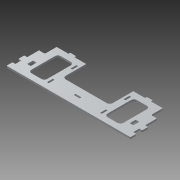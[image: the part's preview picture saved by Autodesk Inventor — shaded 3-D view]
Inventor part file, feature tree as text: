
AUTODESK INVENTOR PART (.ipt)
format: ipt  version: 2015 (Build 190159000, 159)  size: 278,016 bytes
history: native  units: mm
features: extrude x1, sketch x1
ambient origin geometry x8: Origin, YZ Plane, XZ Plane, XY Plane, X Axis, Y Axis, Z Axis, Center Point
bodies: Body1 (feature_tree)
feature tree (2):
  extrude  "Extrusion8"  Depth=40.0mm
  sketch  "Sketch1"  dims[d0=80.0mm d1=40.0mm d2=50.0mm d10=50.0mm d15=3.0mm d16=10.0mm d18=10.0mm d20=3.0mm d23=40.0mm d24=40.0mm d27=1.0mm d28=10.0mm d29=6.0mm d31=40.0mm d32=10.0mm d33=6.0mm d35=40.0mm d39=10.0mm d40=3.0mm d41=10.0mm d42=3.0mm d44=10.0mm d45=10.0mm d50=3.0mm d51=10.0mm d52=10.0mm d54=3.0mm d55=10.0mm d56=10.0mm d60=10.0mm d61=3.0mm d62=17.0mm d66=40.0mm d67=40.0mm d71=3.5mm d72=3.5mm d73=3.5mm d74=3.5mm d77=20.0mm d78=20.0mm d79=10.0mm d80=10.0mm d81=2.0mm d82=10.0mm d84=50.0mm d85=20.0mm d86=20.0mm d87=60.0mm d88=5.0mm d92=30.0mm d93=5.0mm d94=30.0mm d95=1.0mm d96=5.0mm d97=10.0mm d98=10.0mm d99=1.0mm d100=10.0mm d101=10.0mm d102=5.0mm d103=5.0mm d104=210.0mm d105=1.0mm d106=5.0mm d107=70.0mm d108=5.0mm d109=27.0mm d110=50.0mm d111=10.0mm d112=12.0mm d113=50.0mm d114=27.0mm d115=12.0mm d116=10.0mm d117=5.0mm d118=3.0mm d119=0.0mm]
